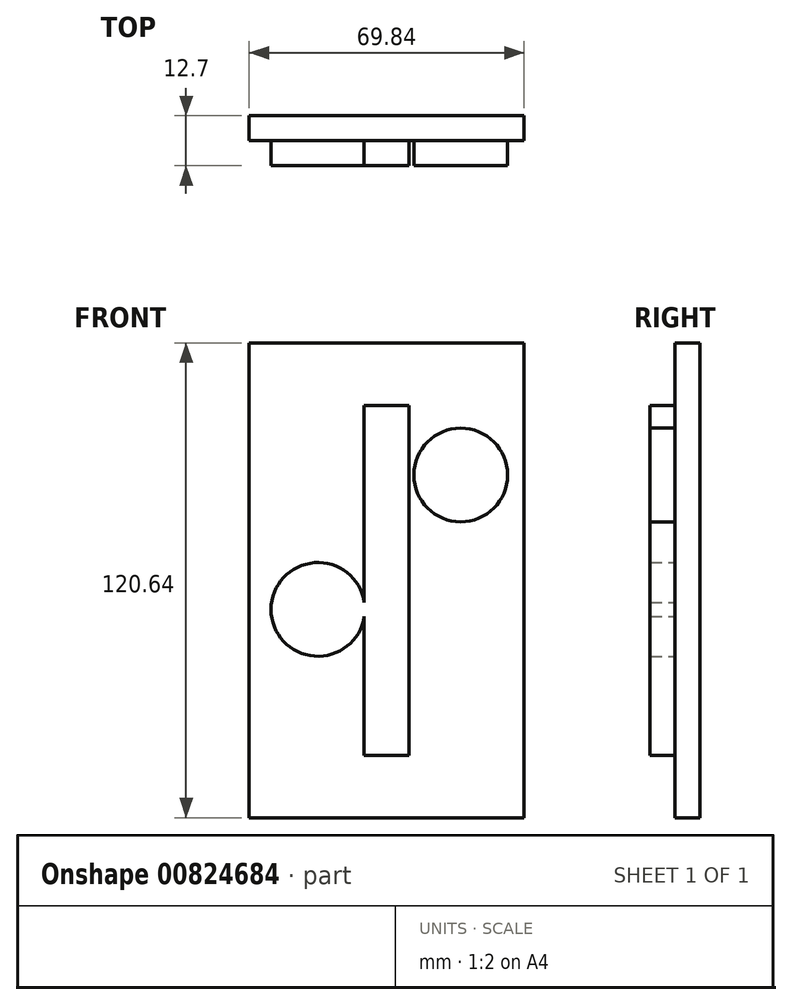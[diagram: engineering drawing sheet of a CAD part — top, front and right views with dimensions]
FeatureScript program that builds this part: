
annotation { "Feature Type Name" : "Feature", "Feature Type Description" : "" }
export const myFeature = defineFeature(function(context is Context, id is Id, definition is map)
    precondition{}
    {
        {
            var Q0;
            Q0=qCreatedBy(makeId("Front.planeOp"),FACE);
            var sketch = newSketch(context, id + "F0", { "sketchPlane" : qUnion([Q0])});
            skLineSegment(sketch, "E0.bottom", {"start": v(34.93, -60.33) * mm, "end": v(-34.92, -60.33) * mm});
            skLineSegment(sketch, "E0.top", {"start": v(34.92, 60.33) * mm, "end": v(-34.93, 60.32) * mm});
            skLineSegment(sketch, "E0.left", {"start": v(34.93, -60.33) * mm, "end": v(34.92, 60.33) * mm});
            skLineSegment(sketch, "E0.right", {"start": v(-34.92, -60.33) * mm, "end": v(-34.93, 60.32) * mm});
            skPoint(sketch, "E0.middle", {"position": v(0, 0) * mm});
            skLineSegment(sketch, "E1.bottom", {"start": v(4.76, -12.7) * mm, "end": v(-4.76, -12.7) * mm});
            skLineSegment(sketch, "E1.top", {"start": v(4.76, 12.7) * mm, "end": v(-4.76, 12.7) * mm});
            skLineSegment(sketch, "E1.left", {"start": v(4.76, -12.7) * mm, "end": v(4.76, 12.7) * mm});
            skLineSegment(sketch, "E1.right", {"start": v(-4.76, -12.7) * mm, "end": v(-4.76, 12.7) * mm});
            skSolve(sketch);
        }
        {
            var Q0;
            Q0=makeQuery(id+"F0.imprint","IMPRINT",FACE,{"disambiguationData":[TD([[makeQuery(id+"F0.imprint","IMPRINT",EDGE,{"derivedFrom":sQuery(id+"F0.wireOp",EDGE,"E0.bottom")}),-1.0]])]});
            extrude(context, id + "F1", {"entities" : qUnion([Q0]), "depth" : 6.35 * mm, "offsetDistance" : 25.4 * mm});
        }
        {
            var Q0;
            Q0=qCreatedBy(makeId("Front.planeOp"),FACE);
            var sketch = newSketch(context, id + "F2", { "sketchPlane" : qUnion([Q0])});
            skCircle(sketch, "E2", {"center": v(-17.48, -7.4) * mm, "radius": 11.9 * mm});
            skSolve(sketch);
        }
        {
            var Q0;
            Q0=qCreatedBy(makeId("Front.planeOp"),FACE);
            var sketch = newSketch(context, id + "F3", { "sketchPlane" : qUnion([Q0])});
            skCircle(sketch, "E3", {"center": v(18.78, 26.75) * mm, "radius": 11.9 * mm});
            skSolve(sketch);
        }
        {
            var Q0;
            Q0 = qSketchRegion(id + "F3", true);
            extrude(context, id + "F4", {"entities" : qUnion([Q0]), "operationType" : NewBodyOperationType.ADD, "depth" : 12.7 * mm, "offsetDistance" : 25.4 * mm});
        }
        {
            var Q0;
            Q0 = qSketchRegion(id + "F2", true);
            extrude(context, id + "F5", {"entities" : qUnion([Q0]), "operationType" : NewBodyOperationType.ADD, "depth" : 12.7 * mm, "offsetDistance" : 25.4 * mm});
        }
        {
            var Q0;
            Q0=qCreatedBy(makeId("Front.planeOp"),FACE);
            var sketch = newSketch(context, id + "F6", { "sketchPlane" : qUnion([Q0])});
            skLineSegment(sketch, "E4.bottom", {"start": v(5.71, -44.45) * mm, "end": v(-5.72, -44.45) * mm});
            skLineSegment(sketch, "E4.top", {"start": v(5.72, 44.45) * mm, "end": v(-5.71, 44.45) * mm});
            skLineSegment(sketch, "E4.left", {"start": v(5.71, -44.45) * mm, "end": v(5.72, 44.45) * mm});
            skLineSegment(sketch, "E4.right", {"start": v(-5.72, -44.45) * mm, "end": v(-5.71, 44.45) * mm});
            skPoint(sketch, "E4.middle", {"position": v(0, 0) * mm});
            skSolve(sketch);
        }
        {
            var Q0;
            Q0 = qSketchRegion(id + "F6", true);
            extrude(context, id + "F7", {"entities" : qUnion([Q0]), "operationType" : NewBodyOperationType.ADD, "depth" : 12.7 * mm, "offsetDistance" : 25.4 * mm});
        }
    });
